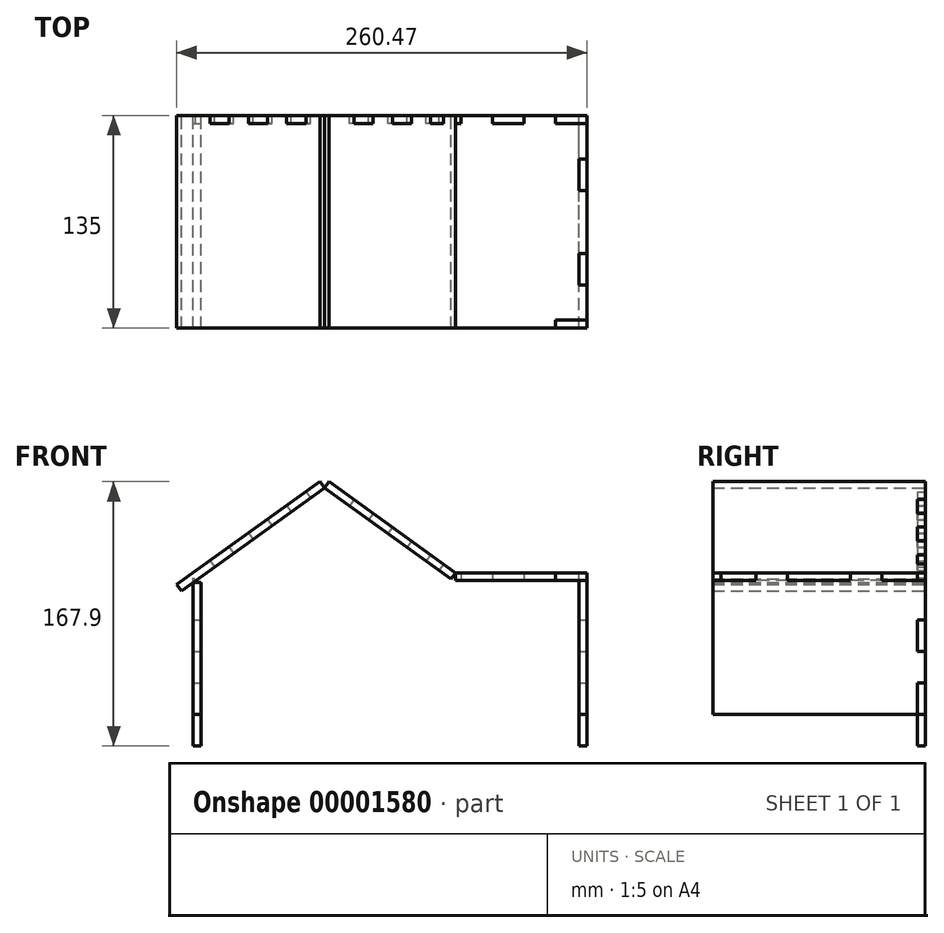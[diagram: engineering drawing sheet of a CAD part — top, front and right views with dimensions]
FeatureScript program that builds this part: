
annotation { "Feature Type Name" : "Feature", "Feature Type Description" : "" }
export const myFeature = defineFeature(function(context is Context, id is Id, definition is map)
    precondition{}
    {
        {
            var Q0;
            Q0=qCreatedBy(makeId("Front.planeOp"),FACE);
            var sketch = newSketch(context, id + "F0", { "sketchPlane" : qUnion([Q0])});
            skLineSegment(sketch, "E0.bottom", {"start": v(0, 0) * mm, "end": v(250, 0) * mm});
            skLineSegment(sketch, "E0.left", {"start": v(0, 0) * mm, "end": v(0, 103.84) * mm});
            skLineSegment(sketch, "E0.right", {"start": v(250, 0) * mm, "end": v(250, 110) * mm});
            skLineSegment(sketch, "E1.0", {"start": v(83.33, 0) * mm, "end": v(83.33, 170) * mm, "construction": true});
            skLineSegment(sketch, "E2.0", {"start": v(166.67, 0) * mm, "end": v(166.67, 110) * mm, "construction": true});
            skLineSegment(sketch, "E3", {"start": v(166.67, 110) * mm, "end": v(86.25, 167.9) * mm});
            skLineSegment(sketch, "E4", {"start": v(80.41, 167.9) * mm, "end": v(-10.47, 102.46) * mm});
            skLineSegment(sketch, "E5.trimOffspring", {"start": v(166.67, 110) * mm, "end": v(250, 110) * mm});
            skLineSegment(sketch, "E6.0", {"start": v(5, 0) * mm, "end": v(5, 103.84) * mm});
            skLineSegment(sketch, "E6.1", {"start": v(83.33, 163.84) * mm, "end": v(-7.55, 98.4) * mm});
            skLineSegment(sketch, "E6.2", {"start": v(163.75, 105.94) * mm, "end": v(83.33, 163.84) * mm});
            skLineSegment(sketch, "E6.3", {"start": v(166.67, 105) * mm, "end": v(245, 105) * mm});
            skLineSegment(sketch, "E6.4", {"start": v(245, 0) * mm, "end": v(245, 105) * mm});
            skLineSegment(sketch, "E7", {"start": v(245, 105) * mm, "end": v(250, 105) * mm});
            skLineSegment(sketch, "E8", {"start": v(166.67, 110) * mm, "end": v(166.67, 105) * mm});
            skLineSegment(sketch, "E9", {"start": v(166.67, 110) * mm, "end": v(163.75, 105.94) * mm});
            skLineSegment(sketch, "E10", {"start": v(0, 103.84) * mm, "end": v(5, 103.84) * mm});
            skLineSegment(sketch, "E11", {"start": v(245, 0) * mm, "end": v(250, 0) * mm});
            skLineSegment(sketch, "E12.0", {"start": v(-10.47, 102.46) * mm, "end": v(-7.55, 98.4) * mm});
            skLineSegment(sketch, "E13", {"start": v(0, 103.84) * mm, "end": v(0, 110) * mm});
            skLineSegment(sketch, "E14", {"start": v(245, 105) * mm, "end": v(245, 110) * mm});
            skLineSegment(sketch, "E15.0", {"start": v(0, 55) * mm, "end": v(250, 55) * mm, "construction": true});
            skLineSegment(sketch, "E16.0.1.0", {"start": v(245, 20) * mm, "end": v(250, 20) * mm});
            skLineSegment(sketch, "E16.0.2.0", {"start": v(245, 40) * mm, "end": v(250, 40) * mm});
            skLineSegment(sketch, "E16.0.3.0", {"start": v(245, 60) * mm, "end": v(250, 60) * mm});
            skLineSegment(sketch, "E16.0.4.0", {"start": v(245, 80) * mm, "end": v(250, 80) * mm});
            skLineSegment(sketch, "E16.direction1", {"start": v(245, 0) * mm, "end": v(270, 0) * mm, "construction": true});
            skLineSegment(sketch, "E16.direction2", {"start": v(245, 0) * mm, "end": v(245, 20) * mm, "construction": true});
            skLineSegment(sketch, "E17", {"start": v(0, 0) * mm, "end": v(5, 0) * mm});
            skLineSegment(sketch, "E18.0.1.0", {"start": v(0, 20) * mm, "end": v(5, 20) * mm});
            skLineSegment(sketch, "E18.0.2.0", {"start": v(0, 40) * mm, "end": v(5, 40) * mm});
            skLineSegment(sketch, "E18.0.3.0", {"start": v(0, 60) * mm, "end": v(5, 60) * mm});
            skLineSegment(sketch, "E18.0.4.0", {"start": v(0, 80) * mm, "end": v(5, 80) * mm});
            skLineSegment(sketch, "E18.direction1", {"start": v(0, 0) * mm, "end": v(25, 0) * mm, "construction": true});
            skLineSegment(sketch, "E18.direction2", {"start": v(0, 0) * mm, "end": v(0, 20) * mm, "construction": true});
            skLineSegment(sketch, "E19", {"start": v(250, 110) * mm, "end": v(250, 105) * mm});
            skLineSegment(sketch, "E20.1.0.0", {"start": v(230, 110) * mm, "end": v(230, 105) * mm});
            skLineSegment(sketch, "E20.2.0.0", {"start": v(210, 110) * mm, "end": v(210, 105) * mm});
            skLineSegment(sketch, "E20.3.0.0", {"start": v(190, 110) * mm, "end": v(190, 105) * mm});
            skLineSegment(sketch, "E20.4.0.0", {"start": v(170, 110) * mm, "end": v(170, 105) * mm});
            skLineSegment(sketch, "E20.direction1", {"start": v(250, 105) * mm, "end": v(230, 105) * mm, "construction": true});
            skLineSegment(sketch, "E21", {"start": v(83.33, 163.84) * mm, "end": v(86.25, 167.9) * mm});
            skLineSegment(sketch, "E22", {"start": v(83.33, 163.84) * mm, "end": v(80.41, 167.9) * mm});
            skLineSegment(sketch, "E23", {"start": v(126.46, 138.95) * mm, "end": v(123.54, 134.9) * mm});
            skLineSegment(sketch, "E24", {"start": v(34.97, 135.18) * mm, "end": v(37.9, 131.12) * mm});
            skLineSegment(sketch, "E25.0", {"start": v(114.29, 147.71) * mm, "end": v(111.37, 143.66) * mm});
            skLineSegment(sketch, "E26.0", {"start": v(102.11, 156.48) * mm, "end": v(99.2, 152.42) * mm});
            skLineSegment(sketch, "E27.0.MirrorCS", {"start": v(138.63, 130.18) * mm, "end": v(135.71, 126.13) * mm});
            skLineSegment(sketch, "E28.0.MirrorCS", {"start": v(150.8, 121.42) * mm, "end": v(147.89, 117.36) * mm});
            skLineSegment(sketch, "E29.0", {"start": v(22.8, 126.41) * mm, "end": v(25.72, 122.36) * mm});
            skLineSegment(sketch, "E30.0", {"start": v(10.62, 117.65) * mm, "end": v(13.55, 113.6) * mm});
            skLineSegment(sketch, "E31.0", {"start": v(-1.55, 108.89) * mm, "end": v(1.37, 104.83) * mm});
            skLineSegment(sketch, "E32.0.MirrorCS", {"start": v(47.14, 143.94) * mm, "end": v(50.07, 139.89) * mm});
            skLineSegment(sketch, "E33.0.MirrorCS", {"start": v(59.32, 152.7) * mm, "end": v(62.24, 148.65) * mm});
            skLineSegment(sketch, "E34.0.MirrorCS", {"start": v(71.49, 161.47) * mm, "end": v(74.41, 157.42) * mm});
            skLineSegment(sketch, "E35.0", {"start": v(158.92, 115.58) * mm, "end": v(156, 111.52) * mm});
            skSolve(sketch);
        }
        {
            var Q0;
            {var subQ1=sQuery(id+"F0.wireOp",EDGE,"E8");Q0=makeQuery(id+"F0.imprint","IMPRINT",FACE,{"disambiguationData":[TD([[makeQuery(id+"F0.imprint","IMPRINT",EDGE,{"derivedFrom":subQ1}),1.0]])]});}
            var Q1;
            {var subQ1=sQuery(id+"F0.wireOp",EDGE,"E20.2.0.0");Q1=makeQuery(id+"F0.imprint","IMPRINT",FACE,{"disambiguationData":[TD([[makeQuery(id+"F0.imprint","IMPRINT",EDGE,{"derivedFrom":subQ1}),-1.0]])]});}
            var Q2;
            {var subQ1=sQuery(id+"F0.wireOp",EDGE,"E18.0.1.0");Q2=makeQuery(id+"F0.imprint","IMPRINT",FACE,{"disambiguationData":[TD([[makeQuery(id+"F0.imprint","IMPRINT",EDGE,{"derivedFrom":subQ1}),1.0]])]});}
            var Q3;
            {var subQ1=sQuery(id+"F0.wireOp",EDGE,"E18.0.3.0");Q3=makeQuery(id+"F0.imprint","IMPRINT",FACE,{"disambiguationData":[TD([[makeQuery(id+"F0.imprint","IMPRINT",EDGE,{"derivedFrom":subQ1}),1.0]])]});}
            var Q4;
            {var subQ1=sQuery(id+"F0.wireOp",EDGE,"E16.0.1.0");Q4=makeQuery(id+"F0.imprint","IMPRINT",FACE,{"disambiguationData":[TD([[makeQuery(id+"F0.imprint","IMPRINT",EDGE,{"derivedFrom":subQ1}),1.0]])]});}
            var Q5;
            {var subQ2=sQuery(id+"F0.wireOp",EDGE,"E16.0.3.0");Q5=makeQuery(id+"F0.imprint","IMPRINT",FACE,{"disambiguationData":[TD([[makeQuery(id+"F0.imprint","IMPRINT",EDGE,{"derivedFrom":subQ2}),1.0]])]});}
            var Q6;
            {var subQ13=sQuery(id+"F0.wireOp",EDGE,"E0.bottom");Q6=makeQuery(id+"F0.imprint","IMPRINT",FACE,{"disambiguationData":[TD([[makeQuery(id+"F0.imprint","IMPRINT",EDGE,{"derivedFrom":subQ13}),1.0]])]});}
            var Q7;
            {var subQ0=sQuery(id+"F0.wireOp",EDGE,"E14");Q7=makeQuery(id+"F0.imprint","IMPRINT",FACE,{"disambiguationData":[TD([[makeQuery(id+"F0.imprint","IMPRINT",EDGE,{"derivedFrom":subQ0}),1.0]])]});}
            var Q8;
            Q8=makeQuery(id+"F0.imprint","IMPRINT",FACE,{"disambiguationData":[TD([[makeQuery(id+"F0.imprint","IMPRINT",EDGE,{"derivedFrom":sQuery(id+"F0.wireOp",EDGE,"E7")}),1.0]])]});
            var Q9;
            {var subQ0=sQuery(id+"F0.wireOp",EDGE,"E31.0");var subQ3=sQuery(id+"F0.wireOp",EDGE,"E6.1");var subQ4=makeQuery(id+"F0.imprint","INTERSECT",VERTEX,{"derivedFrom":[subQ3,subQ0]});Q9=makeQuery(id+"F0.imprint","IMPRINT",FACE,{"disambiguationData":[TD([[makeQuery(id+"F0.imprint","IMPRINT",EDGE,{"disambiguationData":[TD([[subQ4,1.0]])],"derivedFrom":subQ0}),-1.0]])]});}
            var Q10;
            {var subQ1=sQuery(id+"F0.wireOp",EDGE,"E33.0.MirrorCS");Q10=makeQuery(id+"F0.imprint","IMPRINT",FACE,{"disambiguationData":[TD([[makeQuery(id+"F0.imprint","IMPRINT",EDGE,{"derivedFrom":subQ1}),1.0]])]});}
            var Q11;
            {var subQ1=sQuery(id+"F0.wireOp",EDGE,"E24");Q11=makeQuery(id+"F0.imprint","IMPRINT",FACE,{"disambiguationData":[TD([[makeQuery(id+"F0.imprint","IMPRINT",EDGE,{"derivedFrom":subQ1}),1.0]])]});}
            var Q12;
            {var subQ1=sQuery(id+"F0.wireOp",EDGE,"E29.0");Q12=makeQuery(id+"F0.imprint","IMPRINT",FACE,{"disambiguationData":[TD([[makeQuery(id+"F0.imprint","IMPRINT",EDGE,{"derivedFrom":subQ1}),-1.0]])]});}
            var Q13;
            {var subQ1=sQuery(id+"F0.wireOp",EDGE,"E25.0");Q13=makeQuery(id+"F0.imprint","IMPRINT",FACE,{"disambiguationData":[TD([[makeQuery(id+"F0.imprint","IMPRINT",EDGE,{"derivedFrom":subQ1}),-1.0]])]});}
            var Q14;
            {var subQ1=sQuery(id+"F0.wireOp",EDGE,"E23");Q14=makeQuery(id+"F0.imprint","IMPRINT",FACE,{"disambiguationData":[TD([[makeQuery(id+"F0.imprint","IMPRINT",EDGE,{"derivedFrom":subQ1}),1.0]])]});}
            var Q15;
            {var subQ1=sQuery(id+"F0.wireOp",EDGE,"E28.0.MirrorCS");Q15=makeQuery(id+"F0.imprint","IMPRINT",FACE,{"disambiguationData":[TD([[makeQuery(id+"F0.imprint","IMPRINT",EDGE,{"derivedFrom":subQ1}),1.0]])]});}
            extrude(context, id + "F1", {"entities" : qUnion([Q0, Q1, Q2, Q3, Q4, Q5, Q6, Q7, Q8, Q9, Q10, Q11, Q12, Q13, Q14, Q15]), "depth" : 5 * mm});
        }
        {
            var Q0;
            Q0=makeQuery(id+"F1.opExtrude","SWEPT_BODY",BODY,{"disambiguationData":[OSD([sQuery(id+"F0.wireOp",EDGE,"E0.bottom"),sQuery(id+"F0.wireOp",EDGE,"E0.left"),sQuery(id+"F0.wireOp",EDGE,"E0.right"),sQuery(id+"F0.wireOp",EDGE,"E3"),sQuery(id+"F0.wireOp",EDGE,"E4"),sQuery(id+"F0.wireOp",EDGE,"E5.trimOffspring"),sQuery(id+"F0.wireOp",EDGE,"E6.0"),sQuery(id+"F0.wireOp",EDGE,"E6.1"),sQuery(id+"F0.wireOp",EDGE,"E6.2"),sQuery(id+"F0.wireOp",EDGE,"E6.3"),sQuery(id+"F0.wireOp",EDGE,"E6.4"),sQuery(id+"F0.wireOp",EDGE,"E7"),sQuery(id+"F0.wireOp",EDGE,"E9"),sQuery(id+"F0.wireOp",EDGE,"E10"),sQuery(id+"F0.wireOp",EDGE,"E13"),sQuery(id+"F0.wireOp",EDGE,"E16.0.1.0"),sQuery(id+"F0.wireOp",EDGE,"E16.0.2.0"),sQuery(id+"F0.wireOp",EDGE,"E16.0.3.0"),sQuery(id+"F0.wireOp",EDGE,"E16.0.4.0"),sQuery(id+"F0.wireOp",EDGE,"E18.0.1.0"),sQuery(id+"F0.wireOp",EDGE,"E18.0.2.0"),sQuery(id+"F0.wireOp",EDGE,"E18.0.3.0"),sQuery(id+"F0.wireOp",EDGE,"E18.0.4.0"),sQuery(id+"F0.wireOp",EDGE,"E19"),sQuery(id+"F0.wireOp",EDGE,"E20.1.0.0"),sQuery(id+"F0.wireOp",EDGE,"E20.2.0.0"),sQuery(id+"F0.wireOp",EDGE,"E20.3.0.0"),sQuery(id+"F0.wireOp",EDGE,"E20.4.0.0"),sQuery(id+"F0.wireOp",EDGE,"E23"),sQuery(id+"F0.wireOp",EDGE,"E24"),sQuery(id+"F0.wireOp",EDGE,"E25.0"),sQuery(id+"F0.wireOp",EDGE,"E26.0"),sQuery(id+"F0.wireOp",EDGE,"E27.0.MirrorCS"),sQuery(id+"F0.wireOp",EDGE,"E28.0.MirrorCS"),sQuery(id+"F0.wireOp",EDGE,"E29.0"),sQuery(id+"F0.wireOp",EDGE,"E30.0"),sQuery(id+"F0.wireOp",EDGE,"E31.0"),sQuery(id+"F0.wireOp",EDGE,"E32.0.MirrorCS"),sQuery(id+"F0.wireOp",EDGE,"E33.0.MirrorCS"),sQuery(id+"F0.wireOp",EDGE,"E34.0.MirrorCS"),sQuery(id+"F0.wireOp",EDGE,"E35.0")])]});
            transform(context, id + "F2", {"entities" : qUnion([Q0]), "transformType" : TransformType.TRANSLATION_3D, "dx" : 0 * mm, "dy" : -130 * mm, "dz" : 0 * mm, "makeCopy" : true});
        }
        {
            var Q0;
            Q0=makeQuery(id+"F2.opPattern","COPY",FACE,{"derivedFrom":makeQuery(id+"F1.opExtrude","CAP_FACE",FACE,{"disambiguationData":[OSD([sQuery(id+"F0.wireOp",EDGE,"E0.bottom"),sQuery(id+"F0.wireOp",EDGE,"E0.left"),sQuery(id+"F0.wireOp",EDGE,"E0.right"),sQuery(id+"F0.wireOp",EDGE,"E3"),sQuery(id+"F0.wireOp",EDGE,"E4"),sQuery(id+"F0.wireOp",EDGE,"E5.trimOffspring"),sQuery(id+"F0.wireOp",EDGE,"E6.0"),sQuery(id+"F0.wireOp",EDGE,"E6.1"),sQuery(id+"F0.wireOp",EDGE,"E6.2"),sQuery(id+"F0.wireOp",EDGE,"E6.3"),sQuery(id+"F0.wireOp",EDGE,"E6.4"),sQuery(id+"F0.wireOp",EDGE,"E7"),sQuery(id+"F0.wireOp",EDGE,"E9"),sQuery(id+"F0.wireOp",EDGE,"E10"),sQuery(id+"F0.wireOp",EDGE,"E13"),sQuery(id+"F0.wireOp",EDGE,"E16.0.1.0"),sQuery(id+"F0.wireOp",EDGE,"E16.0.2.0"),sQuery(id+"F0.wireOp",EDGE,"E16.0.3.0"),sQuery(id+"F0.wireOp",EDGE,"E16.0.4.0"),sQuery(id+"F0.wireOp",EDGE,"E18.0.1.0"),sQuery(id+"F0.wireOp",EDGE,"E18.0.2.0"),sQuery(id+"F0.wireOp",EDGE,"E18.0.3.0"),sQuery(id+"F0.wireOp",EDGE,"E18.0.4.0"),sQuery(id+"F0.wireOp",EDGE,"E19"),sQuery(id+"F0.wireOp",EDGE,"E20.1.0.0"),sQuery(id+"F0.wireOp",EDGE,"E20.2.0.0"),sQuery(id+"F0.wireOp",EDGE,"E20.3.0.0"),sQuery(id+"F0.wireOp",EDGE,"E20.4.0.0"),sQuery(id+"F0.wireOp",EDGE,"E23"),sQuery(id+"F0.wireOp",EDGE,"E24"),sQuery(id+"F0.wireOp",EDGE,"E25.0"),sQuery(id+"F0.wireOp",EDGE,"E26.0"),sQuery(id+"F0.wireOp",EDGE,"E27.0.MirrorCS"),sQuery(id+"F0.wireOp",EDGE,"E28.0.MirrorCS"),sQuery(id+"F0.wireOp",EDGE,"E29.0"),sQuery(id+"F0.wireOp",EDGE,"E30.0"),sQuery(id+"F0.wireOp",EDGE,"E31.0"),sQuery(id+"F0.wireOp",EDGE,"E32.0.MirrorCS"),sQuery(id+"F0.wireOp",EDGE,"E33.0.MirrorCS"),sQuery(id+"F0.wireOp",EDGE,"E34.0.MirrorCS"),sQuery(id+"F0.wireOp",EDGE,"E35.0")])],"isStart":false}),"instanceName":"1"});
            var sketch = newSketch(context, id + "F3", { "sketchPlane" : qUnion([Q0])});
            skLineSegment(sketch, "E36.0", {"start": v(15, 0) * mm, "end": v(15, 55) * mm});
            skLineSegment(sketch, "E37", {"start": v(15, 0) * mm, "end": v(95, 0) * mm});
            skLineSegment(sketch, "E38", {"start": v(95, 0) * mm, "end": v(95, 50) * mm});
            skArc(sketch, "E39", {"start": v(95, 50) * mm, "mid": v(57.35, 90.08) * mm, "end": v(15, 55) * mm});
            skSolve(sketch);
        }
        {
            var Q0;
            Q0=makeQuery(id+"F3.imprint","IMPRINT",FACE,{"disambiguationData":[TD([[makeQuery(id+"F3.imprint","IMPRINT",EDGE,{"derivedFrom":sQuery(id+"F3.wireOp",EDGE,"E36.0")}),-1.0]])]});
            extrude(context, id + "F4", {"entities" : qUnion([Q0]), "operationType" : NewBodyOperationType.REMOVE, "endBound" : BoundingType.THROUGH_ALL, "oppositeDirection" : true, "depth" : 25 * mm});
        }
        {
            var Q0;
            {var subQ1=sQuery(id+"F0.wireOp",EDGE,"E8");Q0=makeQuery(id+"F0.imprint","IMPRINT",FACE,{"disambiguationData":[TD([[makeQuery(id+"F0.imprint","IMPRINT",EDGE,{"derivedFrom":subQ1}),1.0]])]});}
            var Q1;
            {var subQ1=sQuery(id+"F0.wireOp",EDGE,"E20.3.0.0");Q1=makeQuery(id+"F0.imprint","IMPRINT",FACE,{"disambiguationData":[TD([[makeQuery(id+"F0.imprint","IMPRINT",EDGE,{"derivedFrom":subQ1}),-1.0]])]});}
            var Q2;
            {var subQ1=sQuery(id+"F0.wireOp",EDGE,"E20.2.0.0");Q2=makeQuery(id+"F0.imprint","IMPRINT",FACE,{"disambiguationData":[TD([[makeQuery(id+"F0.imprint","IMPRINT",EDGE,{"derivedFrom":subQ1}),-1.0]])]});}
            var Q3;
            {var subQ1=sQuery(id+"F0.wireOp",EDGE,"E20.1.0.0");Q3=makeQuery(id+"F0.imprint","IMPRINT",FACE,{"disambiguationData":[TD([[makeQuery(id+"F0.imprint","IMPRINT",EDGE,{"derivedFrom":subQ1}),-1.0]])]});}
            var Q4;
            {var subQ0=sQuery(id+"F0.wireOp",EDGE,"E14");Q4=makeQuery(id+"F0.imprint","IMPRINT",FACE,{"disambiguationData":[TD([[makeQuery(id+"F0.imprint","IMPRINT",EDGE,{"derivedFrom":subQ0}),1.0]])]});}
            var Q5;
            Q5=makeQuery(id+"F0.imprint","IMPRINT",FACE,{"disambiguationData":[TD([[makeQuery(id+"F0.imprint","IMPRINT",EDGE,{"derivedFrom":sQuery(id+"F0.wireOp",EDGE,"E7")}),1.0]])]});
            extrude(context, id + "F5", {"entities" : qUnion([Q0, Q1, Q2, Q3, Q4, Q5]), "depth" : 135 * mm});
        }
        {
            var Q0;
            Q0=makeQuery(id+"F1.opExtrude","SWEPT_BODY",BODY,{"disambiguationData":[OSD([sQuery(id+"F0.wireOp",EDGE,"E0.bottom"),sQuery(id+"F0.wireOp",EDGE,"E0.left"),sQuery(id+"F0.wireOp",EDGE,"E0.right"),sQuery(id+"F0.wireOp",EDGE,"E3"),sQuery(id+"F0.wireOp",EDGE,"E4"),sQuery(id+"F0.wireOp",EDGE,"E5.trimOffspring"),sQuery(id+"F0.wireOp",EDGE,"E6.0"),sQuery(id+"F0.wireOp",EDGE,"E6.1"),sQuery(id+"F0.wireOp",EDGE,"E6.2"),sQuery(id+"F0.wireOp",EDGE,"E6.3"),sQuery(id+"F0.wireOp",EDGE,"E6.4"),sQuery(id+"F0.wireOp",EDGE,"E7"),sQuery(id+"F0.wireOp",EDGE,"E9"),sQuery(id+"F0.wireOp",EDGE,"E10"),sQuery(id+"F0.wireOp",EDGE,"E13"),sQuery(id+"F0.wireOp",EDGE,"E16.0.1.0"),sQuery(id+"F0.wireOp",EDGE,"E16.0.2.0"),sQuery(id+"F0.wireOp",EDGE,"E16.0.3.0"),sQuery(id+"F0.wireOp",EDGE,"E16.0.4.0"),sQuery(id+"F0.wireOp",EDGE,"E18.0.1.0"),sQuery(id+"F0.wireOp",EDGE,"E18.0.2.0"),sQuery(id+"F0.wireOp",EDGE,"E18.0.3.0"),sQuery(id+"F0.wireOp",EDGE,"E18.0.4.0"),sQuery(id+"F0.wireOp",EDGE,"E19"),sQuery(id+"F0.wireOp",EDGE,"E20.1.0.0"),sQuery(id+"F0.wireOp",EDGE,"E20.2.0.0"),sQuery(id+"F0.wireOp",EDGE,"E20.3.0.0"),sQuery(id+"F0.wireOp",EDGE,"E20.4.0.0"),sQuery(id+"F0.wireOp",EDGE,"E23"),sQuery(id+"F0.wireOp",EDGE,"E24"),sQuery(id+"F0.wireOp",EDGE,"E25.0"),sQuery(id+"F0.wireOp",EDGE,"E26.0"),sQuery(id+"F0.wireOp",EDGE,"E27.0.MirrorCS"),sQuery(id+"F0.wireOp",EDGE,"E28.0.MirrorCS"),sQuery(id+"F0.wireOp",EDGE,"E29.0"),sQuery(id+"F0.wireOp",EDGE,"E30.0"),sQuery(id+"F0.wireOp",EDGE,"E31.0"),sQuery(id+"F0.wireOp",EDGE,"E32.0.MirrorCS"),sQuery(id+"F0.wireOp",EDGE,"E33.0.MirrorCS"),sQuery(id+"F0.wireOp",EDGE,"E34.0.MirrorCS"),sQuery(id+"F0.wireOp",EDGE,"E35.0")])]});
            var Q1;
            Q1=makeQuery(id+"F2.opPattern","COPY",BODY,{"derivedFrom":makeQuery(id+"F1.opExtrude","SWEPT_BODY",BODY,{"disambiguationData":[OSD([sQuery(id+"F0.wireOp",EDGE,"E0.bottom"),sQuery(id+"F0.wireOp",EDGE,"E0.left"),sQuery(id+"F0.wireOp",EDGE,"E0.right"),sQuery(id+"F0.wireOp",EDGE,"E3"),sQuery(id+"F0.wireOp",EDGE,"E4"),sQuery(id+"F0.wireOp",EDGE,"E5.trimOffspring"),sQuery(id+"F0.wireOp",EDGE,"E6.0"),sQuery(id+"F0.wireOp",EDGE,"E6.1"),sQuery(id+"F0.wireOp",EDGE,"E6.2"),sQuery(id+"F0.wireOp",EDGE,"E6.3"),sQuery(id+"F0.wireOp",EDGE,"E6.4"),sQuery(id+"F0.wireOp",EDGE,"E7"),sQuery(id+"F0.wireOp",EDGE,"E9"),sQuery(id+"F0.wireOp",EDGE,"E10"),sQuery(id+"F0.wireOp",EDGE,"E13"),sQuery(id+"F0.wireOp",EDGE,"E16.0.1.0"),sQuery(id+"F0.wireOp",EDGE,"E16.0.2.0"),sQuery(id+"F0.wireOp",EDGE,"E16.0.3.0"),sQuery(id+"F0.wireOp",EDGE,"E16.0.4.0"),sQuery(id+"F0.wireOp",EDGE,"E18.0.1.0"),sQuery(id+"F0.wireOp",EDGE,"E18.0.2.0"),sQuery(id+"F0.wireOp",EDGE,"E18.0.3.0"),sQuery(id+"F0.wireOp",EDGE,"E18.0.4.0"),sQuery(id+"F0.wireOp",EDGE,"E19"),sQuery(id+"F0.wireOp",EDGE,"E20.1.0.0"),sQuery(id+"F0.wireOp",EDGE,"E20.2.0.0"),sQuery(id+"F0.wireOp",EDGE,"E20.3.0.0"),sQuery(id+"F0.wireOp",EDGE,"E20.4.0.0"),sQuery(id+"F0.wireOp",EDGE,"E23"),sQuery(id+"F0.wireOp",EDGE,"E24"),sQuery(id+"F0.wireOp",EDGE,"E25.0"),sQuery(id+"F0.wireOp",EDGE,"E26.0"),sQuery(id+"F0.wireOp",EDGE,"E27.0.MirrorCS"),sQuery(id+"F0.wireOp",EDGE,"E28.0.MirrorCS"),sQuery(id+"F0.wireOp",EDGE,"E29.0"),sQuery(id+"F0.wireOp",EDGE,"E30.0"),sQuery(id+"F0.wireOp",EDGE,"E31.0"),sQuery(id+"F0.wireOp",EDGE,"E32.0.MirrorCS"),sQuery(id+"F0.wireOp",EDGE,"E33.0.MirrorCS"),sQuery(id+"F0.wireOp",EDGE,"E34.0.MirrorCS"),sQuery(id+"F0.wireOp",EDGE,"E35.0")])]}),"instanceName":"1"});
            var Q2;
            Q2=makeQuery(id+"F5.opExtrude","SWEPT_BODY",BODY,{"disambiguationData":[OSD([sQuery(id+"F0.wireOp",EDGE,"E5.trimOffspring"),sQuery(id+"F0.wireOp",EDGE,"E6.3"),sQuery(id+"F0.wireOp",EDGE,"E7"),sQuery(id+"F0.wireOp",EDGE,"E8"),sQuery(id+"F0.wireOp",EDGE,"E19")])]});
            booleanBodies(context, id + "F6", {"operationType" : BooleanOperationType.SUBTRACTION, "tools" : qUnion([Q0, Q1]), "targets" : qUnion([Q2]), "keepTools" : true});
        }
        {
            var Q0;
            Q0=makeQuery(id+"F5.opExtrude","SWEPT_FACE",FACE,{"disambiguationData":[OSD([sQuery(id+"F0.wireOp",EDGE,"E5.trimOffspring")])]});
            var sketch = newSketch(context, id + "F7", { "sketchPlane" : qUnion([Q0])});
            skLineSegment(sketch, "E40.0", {"start": v(245, -130) * mm, "end": v(245, -5) * mm, "construction": true});
            skLineSegment(sketch, "E41", {"start": v(250, -67.5) * mm, "end": v(245, -67.5) * mm});
            skLineSegment(sketch, "E42.0", {"start": v(250, -47.5) * mm, "end": v(245, -47.5) * mm});
            skLineSegment(sketch, "E43.0", {"start": v(250, -27.5) * mm, "end": v(245, -27.5) * mm});
            skLineSegment(sketch, "E44.0.MirrorCS", {"start": v(250, -87.5) * mm, "end": v(245, -87.5) * mm});
            skLineSegment(sketch, "E45.0.MirrorCS", {"start": v(250, -107.5) * mm, "end": v(245, -107.5) * mm});
            skLineSegment(sketch, "E46", {"start": v(245, -27.5) * mm, "end": v(245, -47.5) * mm});
            skLineSegment(sketch, "E47", {"start": v(250, -47.5) * mm, "end": v(250, -27.5) * mm});
            skLineSegment(sketch, "E48", {"start": v(245, -87.5) * mm, "end": v(245, -107.5) * mm});
            skLineSegment(sketch, "E49", {"start": v(250, -107.5) * mm, "end": v(250, -87.5) * mm});
            skSolve(sketch);
        }
        {
            var Q0;
            Q0=makeQuery(id+"F7.imprint","IMPRINT",FACE,{"disambiguationData":[TD([[makeQuery(id+"F7.imprint","IMPRINT",EDGE,{"derivedFrom":sQuery(id+"F7.wireOp",EDGE,"E44.0.MirrorCS")}),1.0]])]});
            var Q1;
            Q1=makeQuery(id+"F7.imprint","IMPRINT",FACE,{"disambiguationData":[TD([[makeQuery(id+"F7.imprint","IMPRINT",EDGE,{"derivedFrom":sQuery(id+"F7.wireOp",EDGE,"E42.0")}),-1.0]])]});
            extrude(context, id + "F8", {"entities" : qUnion([Q0, Q1]), "operationType" : NewBodyOperationType.REMOVE, "oppositeDirection" : true, "depth" : 25 * mm});
        }
        {
            var Q0;
            Q0=makeQuery(id+"F0.imprint","IMPRINT",FACE,{"disambiguationData":[TD([[makeQuery(id+"F0.imprint","IMPRINT",EDGE,{"derivedFrom":sQuery(id+"F0.wireOp",EDGE,"E7")}),1.0]])]});
            var Q1;
            {var subQ1=sQuery(id+"F0.wireOp",EDGE,"E7");Q1=makeQuery(id+"F0.imprint","IMPRINT",FACE,{"disambiguationData":[TD([[makeQuery(id+"F0.imprint","IMPRINT",EDGE,{"derivedFrom":subQ1}),-1.0]])]});}
            var Q2;
            {var subQ2=sQuery(id+"F0.wireOp",EDGE,"E16.0.3.0");Q2=makeQuery(id+"F0.imprint","IMPRINT",FACE,{"disambiguationData":[TD([[makeQuery(id+"F0.imprint","IMPRINT",EDGE,{"derivedFrom":subQ2}),1.0]])]});}
            var Q3;
            {var subQ2=sQuery(id+"F0.wireOp",EDGE,"E16.0.2.0");Q3=makeQuery(id+"F0.imprint","IMPRINT",FACE,{"disambiguationData":[TD([[makeQuery(id+"F0.imprint","IMPRINT",EDGE,{"derivedFrom":subQ2}),1.0]])]});}
            var Q4;
            {var subQ1=sQuery(id+"F0.wireOp",EDGE,"E16.0.1.0");Q4=makeQuery(id+"F0.imprint","IMPRINT",FACE,{"disambiguationData":[TD([[makeQuery(id+"F0.imprint","IMPRINT",EDGE,{"derivedFrom":subQ1}),1.0]])]});}
            var Q5;
            {var subQ1=sQuery(id+"F0.wireOp",EDGE,"E11");Q5=makeQuery(id+"F0.imprint","IMPRINT",FACE,{"disambiguationData":[TD([[makeQuery(id+"F0.imprint","IMPRINT",EDGE,{"derivedFrom":subQ1}),1.0]])]});}
            extrude(context, id + "F9", {"entities" : qUnion([Q0, Q1, Q2, Q3, Q4, Q5]), "depth" : 135 * mm});
        }
        {
            var Q0;
            Q0=makeQuery(id+"F2.opPattern","COPY",BODY,{"derivedFrom":makeQuery(id+"F1.opExtrude","SWEPT_BODY",BODY,{"disambiguationData":[OSD([sQuery(id+"F0.wireOp",EDGE,"E0.bottom"),sQuery(id+"F0.wireOp",EDGE,"E0.left"),sQuery(id+"F0.wireOp",EDGE,"E0.right"),sQuery(id+"F0.wireOp",EDGE,"E3"),sQuery(id+"F0.wireOp",EDGE,"E4"),sQuery(id+"F0.wireOp",EDGE,"E5.trimOffspring"),sQuery(id+"F0.wireOp",EDGE,"E6.0"),sQuery(id+"F0.wireOp",EDGE,"E6.1"),sQuery(id+"F0.wireOp",EDGE,"E6.2"),sQuery(id+"F0.wireOp",EDGE,"E6.3"),sQuery(id+"F0.wireOp",EDGE,"E6.4"),sQuery(id+"F0.wireOp",EDGE,"E7"),sQuery(id+"F0.wireOp",EDGE,"E9"),sQuery(id+"F0.wireOp",EDGE,"E10"),sQuery(id+"F0.wireOp",EDGE,"E13"),sQuery(id+"F0.wireOp",EDGE,"E16.0.1.0"),sQuery(id+"F0.wireOp",EDGE,"E16.0.2.0"),sQuery(id+"F0.wireOp",EDGE,"E16.0.3.0"),sQuery(id+"F0.wireOp",EDGE,"E16.0.4.0"),sQuery(id+"F0.wireOp",EDGE,"E18.0.1.0"),sQuery(id+"F0.wireOp",EDGE,"E18.0.2.0"),sQuery(id+"F0.wireOp",EDGE,"E18.0.3.0"),sQuery(id+"F0.wireOp",EDGE,"E18.0.4.0"),sQuery(id+"F0.wireOp",EDGE,"E19"),sQuery(id+"F0.wireOp",EDGE,"E20.1.0.0"),sQuery(id+"F0.wireOp",EDGE,"E20.2.0.0"),sQuery(id+"F0.wireOp",EDGE,"E20.3.0.0"),sQuery(id+"F0.wireOp",EDGE,"E20.4.0.0"),sQuery(id+"F0.wireOp",EDGE,"E23"),sQuery(id+"F0.wireOp",EDGE,"E24"),sQuery(id+"F0.wireOp",EDGE,"E25.0"),sQuery(id+"F0.wireOp",EDGE,"E26.0"),sQuery(id+"F0.wireOp",EDGE,"E27.0.MirrorCS"),sQuery(id+"F0.wireOp",EDGE,"E28.0.MirrorCS"),sQuery(id+"F0.wireOp",EDGE,"E29.0"),sQuery(id+"F0.wireOp",EDGE,"E30.0"),sQuery(id+"F0.wireOp",EDGE,"E31.0"),sQuery(id+"F0.wireOp",EDGE,"E32.0.MirrorCS"),sQuery(id+"F0.wireOp",EDGE,"E33.0.MirrorCS"),sQuery(id+"F0.wireOp",EDGE,"E34.0.MirrorCS"),sQuery(id+"F0.wireOp",EDGE,"E35.0")])]}),"instanceName":"1"});
            var Q1;
            Q1=makeQuery(id+"F5.opExtrude","SWEPT_BODY",BODY,{"disambiguationData":[OSD([sQuery(id+"F0.wireOp",EDGE,"E5.trimOffspring"),sQuery(id+"F0.wireOp",EDGE,"E6.3"),sQuery(id+"F0.wireOp",EDGE,"E7"),sQuery(id+"F0.wireOp",EDGE,"E8"),sQuery(id+"F0.wireOp",EDGE,"E19")])]});
            var Q2;
            Q2=makeQuery(id+"F1.opExtrude","SWEPT_BODY",BODY,{"disambiguationData":[OSD([sQuery(id+"F0.wireOp",EDGE,"E0.bottom"),sQuery(id+"F0.wireOp",EDGE,"E0.left"),sQuery(id+"F0.wireOp",EDGE,"E0.right"),sQuery(id+"F0.wireOp",EDGE,"E3"),sQuery(id+"F0.wireOp",EDGE,"E4"),sQuery(id+"F0.wireOp",EDGE,"E5.trimOffspring"),sQuery(id+"F0.wireOp",EDGE,"E6.0"),sQuery(id+"F0.wireOp",EDGE,"E6.1"),sQuery(id+"F0.wireOp",EDGE,"E6.2"),sQuery(id+"F0.wireOp",EDGE,"E6.3"),sQuery(id+"F0.wireOp",EDGE,"E6.4"),sQuery(id+"F0.wireOp",EDGE,"E7"),sQuery(id+"F0.wireOp",EDGE,"E9"),sQuery(id+"F0.wireOp",EDGE,"E10"),sQuery(id+"F0.wireOp",EDGE,"E13"),sQuery(id+"F0.wireOp",EDGE,"E16.0.1.0"),sQuery(id+"F0.wireOp",EDGE,"E16.0.2.0"),sQuery(id+"F0.wireOp",EDGE,"E16.0.3.0"),sQuery(id+"F0.wireOp",EDGE,"E16.0.4.0"),sQuery(id+"F0.wireOp",EDGE,"E18.0.1.0"),sQuery(id+"F0.wireOp",EDGE,"E18.0.2.0"),sQuery(id+"F0.wireOp",EDGE,"E18.0.3.0"),sQuery(id+"F0.wireOp",EDGE,"E18.0.4.0"),sQuery(id+"F0.wireOp",EDGE,"E19"),sQuery(id+"F0.wireOp",EDGE,"E20.1.0.0"),sQuery(id+"F0.wireOp",EDGE,"E20.2.0.0"),sQuery(id+"F0.wireOp",EDGE,"E20.3.0.0"),sQuery(id+"F0.wireOp",EDGE,"E20.4.0.0"),sQuery(id+"F0.wireOp",EDGE,"E23"),sQuery(id+"F0.wireOp",EDGE,"E24"),sQuery(id+"F0.wireOp",EDGE,"E25.0"),sQuery(id+"F0.wireOp",EDGE,"E26.0"),sQuery(id+"F0.wireOp",EDGE,"E27.0.MirrorCS"),sQuery(id+"F0.wireOp",EDGE,"E28.0.MirrorCS"),sQuery(id+"F0.wireOp",EDGE,"E29.0"),sQuery(id+"F0.wireOp",EDGE,"E30.0"),sQuery(id+"F0.wireOp",EDGE,"E31.0"),sQuery(id+"F0.wireOp",EDGE,"E32.0.MirrorCS"),sQuery(id+"F0.wireOp",EDGE,"E33.0.MirrorCS"),sQuery(id+"F0.wireOp",EDGE,"E34.0.MirrorCS"),sQuery(id+"F0.wireOp",EDGE,"E35.0")])]});
            var Q3;
            Q3=makeQuery(id+"F9.opExtrude","SWEPT_BODY",BODY,{"disambiguationData":[OSD([sQuery(id+"F0.wireOp",EDGE,"E0.right"),sQuery(id+"F0.wireOp",EDGE,"E5.trimOffspring"),sQuery(id+"F0.wireOp",EDGE,"E6.4"),sQuery(id+"F0.wireOp",EDGE,"E11"),sQuery(id+"F0.wireOp",EDGE,"E14"),sQuery(id+"F0.wireOp",EDGE,"E19")])]});
            booleanBodies(context, id + "F10", {"operationType" : BooleanOperationType.SUBTRACTION, "tools" : qUnion([Q0, Q1, Q2]), "targets" : qUnion([Q3]), "keepTools" : true});
        }
        {
            var Q0;
            {var subQ1=sQuery(id+"F0.wireOp",EDGE,"E10");Q0=makeQuery(id+"F0.imprint","IMPRINT",FACE,{"disambiguationData":[TD([[makeQuery(id+"F0.imprint","IMPRINT",EDGE,{"derivedFrom":subQ1}),-1.0]])]});}
            var Q1;
            {var subQ1=sQuery(id+"F0.wireOp",EDGE,"E18.0.3.0");Q1=makeQuery(id+"F0.imprint","IMPRINT",FACE,{"disambiguationData":[TD([[makeQuery(id+"F0.imprint","IMPRINT",EDGE,{"derivedFrom":subQ1}),1.0]])]});}
            var Q2;
            {var subQ1=sQuery(id+"F0.wireOp",EDGE,"E18.0.2.0");Q2=makeQuery(id+"F0.imprint","IMPRINT",FACE,{"disambiguationData":[TD([[makeQuery(id+"F0.imprint","IMPRINT",EDGE,{"derivedFrom":subQ1}),1.0]])]});}
            var Q3;
            {var subQ1=sQuery(id+"F0.wireOp",EDGE,"E18.0.1.0");Q3=makeQuery(id+"F0.imprint","IMPRINT",FACE,{"disambiguationData":[TD([[makeQuery(id+"F0.imprint","IMPRINT",EDGE,{"derivedFrom":subQ1}),1.0]])]});}
            var Q4;
            {var subQ1=sQuery(id+"F0.wireOp",EDGE,"E17");Q4=makeQuery(id+"F0.imprint","IMPRINT",FACE,{"disambiguationData":[TD([[makeQuery(id+"F0.imprint","IMPRINT",EDGE,{"derivedFrom":subQ1}),1.0]])]});}
            extrude(context, id + "F11", {"entities" : qUnion([Q0, Q1, Q2, Q3, Q4]), "depth" : 135 * mm});
        }
        {
            var Q0;
            Q0=makeQuery(id+"F1.opExtrude","SWEPT_BODY",BODY,{"disambiguationData":[OSD([sQuery(id+"F0.wireOp",EDGE,"E0.bottom"),sQuery(id+"F0.wireOp",EDGE,"E0.left"),sQuery(id+"F0.wireOp",EDGE,"E0.right"),sQuery(id+"F0.wireOp",EDGE,"E3"),sQuery(id+"F0.wireOp",EDGE,"E4"),sQuery(id+"F0.wireOp",EDGE,"E5.trimOffspring"),sQuery(id+"F0.wireOp",EDGE,"E6.0"),sQuery(id+"F0.wireOp",EDGE,"E6.1"),sQuery(id+"F0.wireOp",EDGE,"E6.2"),sQuery(id+"F0.wireOp",EDGE,"E6.3"),sQuery(id+"F0.wireOp",EDGE,"E6.4"),sQuery(id+"F0.wireOp",EDGE,"E7"),sQuery(id+"F0.wireOp",EDGE,"E9"),sQuery(id+"F0.wireOp",EDGE,"E10"),sQuery(id+"F0.wireOp",EDGE,"E13"),sQuery(id+"F0.wireOp",EDGE,"E16.0.1.0"),sQuery(id+"F0.wireOp",EDGE,"E16.0.2.0"),sQuery(id+"F0.wireOp",EDGE,"E16.0.3.0"),sQuery(id+"F0.wireOp",EDGE,"E16.0.4.0"),sQuery(id+"F0.wireOp",EDGE,"E18.0.1.0"),sQuery(id+"F0.wireOp",EDGE,"E18.0.2.0"),sQuery(id+"F0.wireOp",EDGE,"E18.0.3.0"),sQuery(id+"F0.wireOp",EDGE,"E18.0.4.0"),sQuery(id+"F0.wireOp",EDGE,"E19"),sQuery(id+"F0.wireOp",EDGE,"E20.1.0.0"),sQuery(id+"F0.wireOp",EDGE,"E20.2.0.0"),sQuery(id+"F0.wireOp",EDGE,"E20.3.0.0"),sQuery(id+"F0.wireOp",EDGE,"E20.4.0.0"),sQuery(id+"F0.wireOp",EDGE,"E23"),sQuery(id+"F0.wireOp",EDGE,"E24"),sQuery(id+"F0.wireOp",EDGE,"E25.0"),sQuery(id+"F0.wireOp",EDGE,"E26.0"),sQuery(id+"F0.wireOp",EDGE,"E27.0.MirrorCS"),sQuery(id+"F0.wireOp",EDGE,"E28.0.MirrorCS"),sQuery(id+"F0.wireOp",EDGE,"E29.0"),sQuery(id+"F0.wireOp",EDGE,"E30.0"),sQuery(id+"F0.wireOp",EDGE,"E31.0"),sQuery(id+"F0.wireOp",EDGE,"E32.0.MirrorCS"),sQuery(id+"F0.wireOp",EDGE,"E33.0.MirrorCS"),sQuery(id+"F0.wireOp",EDGE,"E34.0.MirrorCS"),sQuery(id+"F0.wireOp",EDGE,"E35.0")])]});
            var Q1;
            Q1=makeQuery(id+"F2.opPattern","COPY",BODY,{"derivedFrom":makeQuery(id+"F1.opExtrude","SWEPT_BODY",BODY,{"disambiguationData":[OSD([sQuery(id+"F0.wireOp",EDGE,"E0.bottom"),sQuery(id+"F0.wireOp",EDGE,"E0.left"),sQuery(id+"F0.wireOp",EDGE,"E0.right"),sQuery(id+"F0.wireOp",EDGE,"E3"),sQuery(id+"F0.wireOp",EDGE,"E4"),sQuery(id+"F0.wireOp",EDGE,"E5.trimOffspring"),sQuery(id+"F0.wireOp",EDGE,"E6.0"),sQuery(id+"F0.wireOp",EDGE,"E6.1"),sQuery(id+"F0.wireOp",EDGE,"E6.2"),sQuery(id+"F0.wireOp",EDGE,"E6.3"),sQuery(id+"F0.wireOp",EDGE,"E6.4"),sQuery(id+"F0.wireOp",EDGE,"E7"),sQuery(id+"F0.wireOp",EDGE,"E9"),sQuery(id+"F0.wireOp",EDGE,"E10"),sQuery(id+"F0.wireOp",EDGE,"E13"),sQuery(id+"F0.wireOp",EDGE,"E16.0.1.0"),sQuery(id+"F0.wireOp",EDGE,"E16.0.2.0"),sQuery(id+"F0.wireOp",EDGE,"E16.0.3.0"),sQuery(id+"F0.wireOp",EDGE,"E16.0.4.0"),sQuery(id+"F0.wireOp",EDGE,"E18.0.1.0"),sQuery(id+"F0.wireOp",EDGE,"E18.0.2.0"),sQuery(id+"F0.wireOp",EDGE,"E18.0.3.0"),sQuery(id+"F0.wireOp",EDGE,"E18.0.4.0"),sQuery(id+"F0.wireOp",EDGE,"E19"),sQuery(id+"F0.wireOp",EDGE,"E20.1.0.0"),sQuery(id+"F0.wireOp",EDGE,"E20.2.0.0"),sQuery(id+"F0.wireOp",EDGE,"E20.3.0.0"),sQuery(id+"F0.wireOp",EDGE,"E20.4.0.0"),sQuery(id+"F0.wireOp",EDGE,"E23"),sQuery(id+"F0.wireOp",EDGE,"E24"),sQuery(id+"F0.wireOp",EDGE,"E25.0"),sQuery(id+"F0.wireOp",EDGE,"E26.0"),sQuery(id+"F0.wireOp",EDGE,"E27.0.MirrorCS"),sQuery(id+"F0.wireOp",EDGE,"E28.0.MirrorCS"),sQuery(id+"F0.wireOp",EDGE,"E29.0"),sQuery(id+"F0.wireOp",EDGE,"E30.0"),sQuery(id+"F0.wireOp",EDGE,"E31.0"),sQuery(id+"F0.wireOp",EDGE,"E32.0.MirrorCS"),sQuery(id+"F0.wireOp",EDGE,"E33.0.MirrorCS"),sQuery(id+"F0.wireOp",EDGE,"E34.0.MirrorCS"),sQuery(id+"F0.wireOp",EDGE,"E35.0")])]}),"instanceName":"1"});
            var Q2;
            Q2=makeQuery(id+"F11.opExtrude","SWEPT_BODY",BODY,{"disambiguationData":[OSD([sQuery(id+"F0.wireOp",EDGE,"E0.left"),sQuery(id+"F0.wireOp",EDGE,"E6.0"),sQuery(id+"F0.wireOp",EDGE,"E10"),sQuery(id+"F0.wireOp",EDGE,"E17")])]});
            booleanBodies(context, id + "F12", {"operationType" : BooleanOperationType.SUBTRACTION, "tools" : qUnion([Q0, Q1]), "targets" : qUnion([Q2]), "keepTools" : true});
        }
        {
            var Q0;
            {var subQ7=sQuery(id+"F0.wireOp",EDGE,"E12.0");Q0=makeQuery(id+"F0.imprint","IMPRINT",FACE,{"disambiguationData":[TD([[makeQuery(id+"F0.imprint","IMPRINT",EDGE,{"derivedFrom":subQ7}),1.0]])]});}
            var Q1;
            {var subQ1=sQuery(id+"F0.wireOp",EDGE,"E13");var subQ3=sQuery(id+"F0.wireOp",EDGE,"E4");var subQ5=makeQuery(id+"F0.imprint","INTERSECT",VERTEX,{"derivedFrom":[subQ3,subQ1]});Q1=makeQuery(id+"F0.imprint","IMPRINT",FACE,{"disambiguationData":[TD([[makeQuery(id+"F0.imprint","IMPRINT",EDGE,{"disambiguationData":[TD([[subQ5,-1.0]])],"derivedFrom":subQ3}),1.0]])]});}
            var Q2;
            {var subQ0=sQuery(id+"F0.wireOp",EDGE,"E31.0");var subQ3=sQuery(id+"F0.wireOp",EDGE,"E6.1");var subQ4=makeQuery(id+"F0.imprint","INTERSECT",VERTEX,{"derivedFrom":[subQ3,subQ0]});Q2=makeQuery(id+"F0.imprint","IMPRINT",FACE,{"disambiguationData":[TD([[makeQuery(id+"F0.imprint","IMPRINT",EDGE,{"disambiguationData":[TD([[subQ4,1.0]])],"derivedFrom":subQ0}),-1.0]])]});}
            var Q3;
            {var subQ5=sQuery(id+"F0.wireOp",EDGE,"E30.0");Q3=makeQuery(id+"F0.imprint","IMPRINT",FACE,{"disambiguationData":[TD([[makeQuery(id+"F0.imprint","IMPRINT",EDGE,{"derivedFrom":subQ5}),-1.0]])]});}
            var Q4;
            {var subQ1=sQuery(id+"F0.wireOp",EDGE,"E29.0");Q4=makeQuery(id+"F0.imprint","IMPRINT",FACE,{"disambiguationData":[TD([[makeQuery(id+"F0.imprint","IMPRINT",EDGE,{"derivedFrom":subQ1}),-1.0]])]});}
            var Q5;
            {var subQ1=sQuery(id+"F0.wireOp",EDGE,"E24");Q5=makeQuery(id+"F0.imprint","IMPRINT",FACE,{"disambiguationData":[TD([[makeQuery(id+"F0.imprint","IMPRINT",EDGE,{"derivedFrom":subQ1}),-1.0]])]});}
            var Q6;
            {var subQ1=sQuery(id+"F0.wireOp",EDGE,"E24");Q6=makeQuery(id+"F0.imprint","IMPRINT",FACE,{"disambiguationData":[TD([[makeQuery(id+"F0.imprint","IMPRINT",EDGE,{"derivedFrom":subQ1}),1.0]])]});}
            var Q7;
            {var subQ1=sQuery(id+"F0.wireOp",EDGE,"E32.0.MirrorCS");Q7=makeQuery(id+"F0.imprint","IMPRINT",FACE,{"disambiguationData":[TD([[makeQuery(id+"F0.imprint","IMPRINT",EDGE,{"derivedFrom":subQ1}),1.0]])]});}
            var Q8;
            {var subQ1=sQuery(id+"F0.wireOp",EDGE,"E33.0.MirrorCS");Q8=makeQuery(id+"F0.imprint","IMPRINT",FACE,{"disambiguationData":[TD([[makeQuery(id+"F0.imprint","IMPRINT",EDGE,{"derivedFrom":subQ1}),1.0]])]});}
            var Q9;
            {var subQ1=sQuery(id+"F0.wireOp",EDGE,"E22");Q9=makeQuery(id+"F0.imprint","IMPRINT",FACE,{"disambiguationData":[TD([[makeQuery(id+"F0.imprint","IMPRINT",EDGE,{"derivedFrom":subQ1}),1.0]])]});}
            extrude(context, id + "F13", {"entities" : qUnion([Q0, Q1, Q2, Q3, Q4, Q5, Q6, Q7, Q8, Q9]), "depth" : 135 * mm});
        }
        {
            var Q0;
            {var subQ1=sQuery(id+"F0.wireOp",EDGE,"E21");Q0=makeQuery(id+"F0.imprint","IMPRINT",FACE,{"disambiguationData":[TD([[makeQuery(id+"F0.imprint","IMPRINT",EDGE,{"derivedFrom":subQ1}),-1.0]])]});}
            var Q1;
            {var subQ1=sQuery(id+"F0.wireOp",EDGE,"E25.0");Q1=makeQuery(id+"F0.imprint","IMPRINT",FACE,{"disambiguationData":[TD([[makeQuery(id+"F0.imprint","IMPRINT",EDGE,{"derivedFrom":subQ1}),-1.0]])]});}
            var Q2;
            {var subQ1=sQuery(id+"F0.wireOp",EDGE,"E23");Q2=makeQuery(id+"F0.imprint","IMPRINT",FACE,{"disambiguationData":[TD([[makeQuery(id+"F0.imprint","IMPRINT",EDGE,{"derivedFrom":subQ1}),-1.0]])]});}
            var Q3;
            {var subQ1=sQuery(id+"F0.wireOp",EDGE,"E23");Q3=makeQuery(id+"F0.imprint","IMPRINT",FACE,{"disambiguationData":[TD([[makeQuery(id+"F0.imprint","IMPRINT",EDGE,{"derivedFrom":subQ1}),1.0]])]});}
            var Q4;
            {var subQ1=sQuery(id+"F0.wireOp",EDGE,"E27.0.MirrorCS");Q4=makeQuery(id+"F0.imprint","IMPRINT",FACE,{"disambiguationData":[TD([[makeQuery(id+"F0.imprint","IMPRINT",EDGE,{"derivedFrom":subQ1}),1.0]])]});}
            var Q5;
            {var subQ1=sQuery(id+"F0.wireOp",EDGE,"E28.0.MirrorCS");Q5=makeQuery(id+"F0.imprint","IMPRINT",FACE,{"disambiguationData":[TD([[makeQuery(id+"F0.imprint","IMPRINT",EDGE,{"derivedFrom":subQ1}),1.0]])]});}
            var Q6;
            {var subQ1=sQuery(id+"F0.wireOp",EDGE,"E9");Q6=makeQuery(id+"F0.imprint","IMPRINT",FACE,{"disambiguationData":[TD([[makeQuery(id+"F0.imprint","IMPRINT",EDGE,{"derivedFrom":subQ1}),-1.0]])]});}
            extrude(context, id + "F14", {"entities" : qUnion([Q0, Q1, Q2, Q3, Q4, Q5, Q6]), "depth" : 135 * mm});
        }
        {
            var Q0;
            Q0=makeQuery(id+"F2.opPattern","COPY",BODY,{"derivedFrom":makeQuery(id+"F1.opExtrude","SWEPT_BODY",BODY,{"disambiguationData":[OSD([sQuery(id+"F0.wireOp",EDGE,"E0.bottom"),sQuery(id+"F0.wireOp",EDGE,"E0.left"),sQuery(id+"F0.wireOp",EDGE,"E0.right"),sQuery(id+"F0.wireOp",EDGE,"E3"),sQuery(id+"F0.wireOp",EDGE,"E4"),sQuery(id+"F0.wireOp",EDGE,"E5.trimOffspring"),sQuery(id+"F0.wireOp",EDGE,"E6.0"),sQuery(id+"F0.wireOp",EDGE,"E6.1"),sQuery(id+"F0.wireOp",EDGE,"E6.2"),sQuery(id+"F0.wireOp",EDGE,"E6.3"),sQuery(id+"F0.wireOp",EDGE,"E6.4"),sQuery(id+"F0.wireOp",EDGE,"E7"),sQuery(id+"F0.wireOp",EDGE,"E9"),sQuery(id+"F0.wireOp",EDGE,"E10"),sQuery(id+"F0.wireOp",EDGE,"E13"),sQuery(id+"F0.wireOp",EDGE,"E16.0.1.0"),sQuery(id+"F0.wireOp",EDGE,"E16.0.2.0"),sQuery(id+"F0.wireOp",EDGE,"E16.0.3.0"),sQuery(id+"F0.wireOp",EDGE,"E16.0.4.0"),sQuery(id+"F0.wireOp",EDGE,"E18.0.1.0"),sQuery(id+"F0.wireOp",EDGE,"E18.0.2.0"),sQuery(id+"F0.wireOp",EDGE,"E18.0.3.0"),sQuery(id+"F0.wireOp",EDGE,"E18.0.4.0"),sQuery(id+"F0.wireOp",EDGE,"E19"),sQuery(id+"F0.wireOp",EDGE,"E20.1.0.0"),sQuery(id+"F0.wireOp",EDGE,"E20.2.0.0"),sQuery(id+"F0.wireOp",EDGE,"E20.3.0.0"),sQuery(id+"F0.wireOp",EDGE,"E20.4.0.0"),sQuery(id+"F0.wireOp",EDGE,"E23"),sQuery(id+"F0.wireOp",EDGE,"E24"),sQuery(id+"F0.wireOp",EDGE,"E25.0"),sQuery(id+"F0.wireOp",EDGE,"E26.0"),sQuery(id+"F0.wireOp",EDGE,"E27.0.MirrorCS"),sQuery(id+"F0.wireOp",EDGE,"E28.0.MirrorCS"),sQuery(id+"F0.wireOp",EDGE,"E29.0"),sQuery(id+"F0.wireOp",EDGE,"E30.0"),sQuery(id+"F0.wireOp",EDGE,"E31.0"),sQuery(id+"F0.wireOp",EDGE,"E32.0.MirrorCS"),sQuery(id+"F0.wireOp",EDGE,"E33.0.MirrorCS"),sQuery(id+"F0.wireOp",EDGE,"E34.0.MirrorCS"),sQuery(id+"F0.wireOp",EDGE,"E35.0")])]}),"instanceName":"1"});
            var Q1;
            Q1=makeQuery(id+"F1.opExtrude","SWEPT_BODY",BODY,{"disambiguationData":[OSD([sQuery(id+"F0.wireOp",EDGE,"E0.bottom"),sQuery(id+"F0.wireOp",EDGE,"E0.left"),sQuery(id+"F0.wireOp",EDGE,"E0.right"),sQuery(id+"F0.wireOp",EDGE,"E3"),sQuery(id+"F0.wireOp",EDGE,"E4"),sQuery(id+"F0.wireOp",EDGE,"E5.trimOffspring"),sQuery(id+"F0.wireOp",EDGE,"E6.0"),sQuery(id+"F0.wireOp",EDGE,"E6.1"),sQuery(id+"F0.wireOp",EDGE,"E6.2"),sQuery(id+"F0.wireOp",EDGE,"E6.3"),sQuery(id+"F0.wireOp",EDGE,"E6.4"),sQuery(id+"F0.wireOp",EDGE,"E7"),sQuery(id+"F0.wireOp",EDGE,"E9"),sQuery(id+"F0.wireOp",EDGE,"E10"),sQuery(id+"F0.wireOp",EDGE,"E13"),sQuery(id+"F0.wireOp",EDGE,"E16.0.1.0"),sQuery(id+"F0.wireOp",EDGE,"E16.0.2.0"),sQuery(id+"F0.wireOp",EDGE,"E16.0.3.0"),sQuery(id+"F0.wireOp",EDGE,"E16.0.4.0"),sQuery(id+"F0.wireOp",EDGE,"E18.0.1.0"),sQuery(id+"F0.wireOp",EDGE,"E18.0.2.0"),sQuery(id+"F0.wireOp",EDGE,"E18.0.3.0"),sQuery(id+"F0.wireOp",EDGE,"E18.0.4.0"),sQuery(id+"F0.wireOp",EDGE,"E19"),sQuery(id+"F0.wireOp",EDGE,"E20.1.0.0"),sQuery(id+"F0.wireOp",EDGE,"E20.2.0.0"),sQuery(id+"F0.wireOp",EDGE,"E20.3.0.0"),sQuery(id+"F0.wireOp",EDGE,"E20.4.0.0"),sQuery(id+"F0.wireOp",EDGE,"E23"),sQuery(id+"F0.wireOp",EDGE,"E24"),sQuery(id+"F0.wireOp",EDGE,"E25.0"),sQuery(id+"F0.wireOp",EDGE,"E26.0"),sQuery(id+"F0.wireOp",EDGE,"E27.0.MirrorCS"),sQuery(id+"F0.wireOp",EDGE,"E28.0.MirrorCS"),sQuery(id+"F0.wireOp",EDGE,"E29.0"),sQuery(id+"F0.wireOp",EDGE,"E30.0"),sQuery(id+"F0.wireOp",EDGE,"E31.0"),sQuery(id+"F0.wireOp",EDGE,"E32.0.MirrorCS"),sQuery(id+"F0.wireOp",EDGE,"E33.0.MirrorCS"),sQuery(id+"F0.wireOp",EDGE,"E34.0.MirrorCS"),sQuery(id+"F0.wireOp",EDGE,"E35.0")])]});
            var Q2;
            Q2=makeQuery(id+"F13.opExtrude","SWEPT_BODY",BODY,{"disambiguationData":[OSD([sQuery(id+"F0.wireOp",EDGE,"E4"),sQuery(id+"F0.wireOp",EDGE,"E6.1"),sQuery(id+"F0.wireOp",EDGE,"E12.0"),sQuery(id+"F0.wireOp",EDGE,"E22")])]});
            var Q3;
            Q3=makeQuery(id+"F14.opExtrude","SWEPT_BODY",BODY,{"disambiguationData":[OSD([sQuery(id+"F0.wireOp",EDGE,"E3"),sQuery(id+"F0.wireOp",EDGE,"E6.2"),sQuery(id+"F0.wireOp",EDGE,"E9"),sQuery(id+"F0.wireOp",EDGE,"E21")])]});
            booleanBodies(context, id + "F15", {"operationType" : BooleanOperationType.SUBTRACTION, "tools" : qUnion([Q0, Q1]), "targets" : qUnion([Q2, Q3]), "keepTools" : true});
        }
    });
